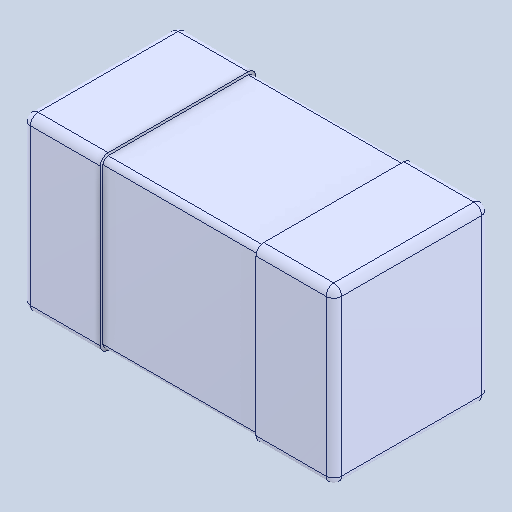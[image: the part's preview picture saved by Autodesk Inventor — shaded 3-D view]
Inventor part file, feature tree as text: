
AUTODESK INVENTOR PART (.ipt)
format: ipt  version: 2025 (Build 290162000, 162)  size: 131,072 bytes
history: native  units: mm
features: fillet x1, mirror x1, other x1
ambient origin geometry x8: Origin, YZ Plane, XZ Plane, XY Plane, X Axis, Y Axis, Z Axis, Center Point
bodies: Solid1 (feature_tree), Solid2 (feature_tree), Solid3 (feature_tree)
feature tree (3):
  fillet  "Fillet1"  [1 undecoded]
  mirror  "Mirror2"
  other  "Boss-Extrude2"
note: 1 required parameter value undecoded (feature->parameter linkage not recoverable at this tier; creation-order binding heuristic only, values carry confidence <= 0.55)
